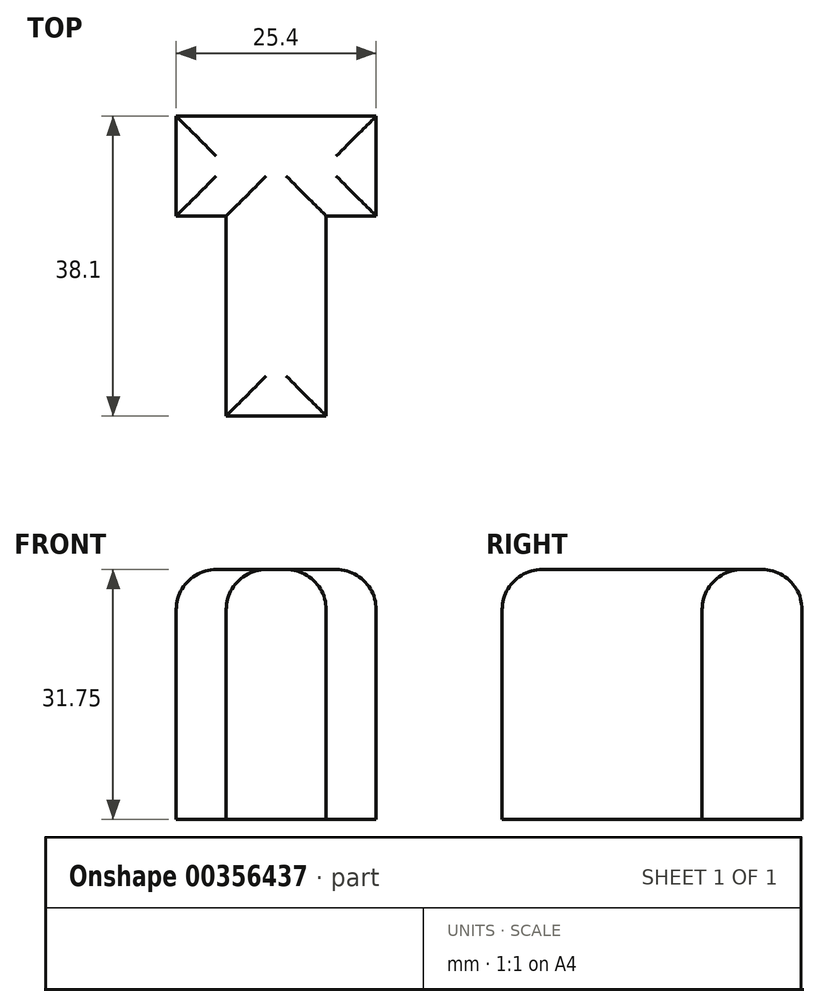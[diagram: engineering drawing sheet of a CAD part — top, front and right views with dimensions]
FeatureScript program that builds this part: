
annotation { "Feature Type Name" : "Feature", "Feature Type Description" : "" }
export const myFeature = defineFeature(function(context is Context, id is Id, definition is map)
    precondition{}
    {
        {
            var Q0;
            Q0=qCreatedBy(makeId("Top.planeOp"),FACE);
            var sketch = newSketch(context, id + "F0", { "sketchPlane" : qUnion([Q0])});
            skLineSegment(sketch, "E0", {"start": v(0, 0) * mm, "end": v(0, 25.4) * mm});
            skLineSegment(sketch, "E1", {"start": v(0, 25.4) * mm, "end": v(-6.35, 25.4) * mm});
            skLineSegment(sketch, "E2", {"start": v(-6.35, 25.4) * mm, "end": v(-6.35, 38.1) * mm});
            skLineSegment(sketch, "E3", {"start": v(-6.35, 38.1) * mm, "end": v(19.05, 38.1) * mm});
            skLineSegment(sketch, "E4", {"start": v(19.05, 38.1) * mm, "end": v(19.05, 25.4) * mm});
            skLineSegment(sketch, "E5", {"start": v(19.05, 25.4) * mm, "end": v(12.7, 25.4) * mm});
            skLineSegment(sketch, "E6", {"start": v(12.7, 25.4) * mm, "end": v(12.7, 0) * mm});
            skLineSegment(sketch, "E7", {"start": v(12.7, 0) * mm, "end": v(0, 0) * mm});
            skSolve(sketch);
        }
        {
            var Q0;
            Q0 = qSketchRegion(id + "F0", true);
            extrude(context, id + "F1", {"entities" : qUnion([Q0]), "oppositeDirection" : true, "depth" : 31.75 * mm});
        }
        {
            var Q0;
            Q0=makeQuery(id+"F1.opExtrude","CAP_EDGE",EDGE,{"disambiguationData":[OSD([sQuery(id+"F0.wireOp",EDGE,"E7")])],"isStart":true});
            var Q1;
            Q1=makeQuery(id+"F1.opExtrude","CAP_EDGE",EDGE,{"disambiguationData":[OSD([sQuery(id+"F0.wireOp",EDGE,"E0")])],"isStart":true});
            var Q2;
            Q2=makeQuery(id+"F1.opExtrude","CAP_EDGE",EDGE,{"disambiguationData":[OSD([sQuery(id+"F0.wireOp",EDGE,"E1")])],"isStart":true});
            var Q3;
            Q3=makeQuery(id+"F1.opExtrude","CAP_EDGE",EDGE,{"disambiguationData":[OSD([sQuery(id+"F0.wireOp",EDGE,"E2")])],"isStart":true});
            var Q4;
            Q4=makeQuery(id+"F1.opExtrude","CAP_EDGE",EDGE,{"disambiguationData":[OSD([sQuery(id+"F0.wireOp",EDGE,"E3")])],"isStart":true});
            var Q5;
            Q5=makeQuery(id+"F1.opExtrude","CAP_EDGE",EDGE,{"disambiguationData":[OSD([sQuery(id+"F0.wireOp",EDGE,"E4")])],"isStart":true});
            var Q6;
            Q6=makeQuery(id+"F1.opExtrude","CAP_EDGE",EDGE,{"disambiguationData":[OSD([sQuery(id+"F0.wireOp",EDGE,"E5")])],"isStart":true});
            var Q7;
            Q7=makeQuery(id+"F1.opExtrude","CAP_EDGE",EDGE,{"disambiguationData":[OSD([sQuery(id+"F0.wireOp",EDGE,"E6")])],"isStart":true});
            fillet(context, id + "F2", {"entities" : qUnion([Q0, Q1, Q2, Q3, Q4, Q5, Q6, Q7]), "radius" : 5.08 * mm, "tangentPropagation" : true, "allowEdgeOverflow" : false});
        }
    });
